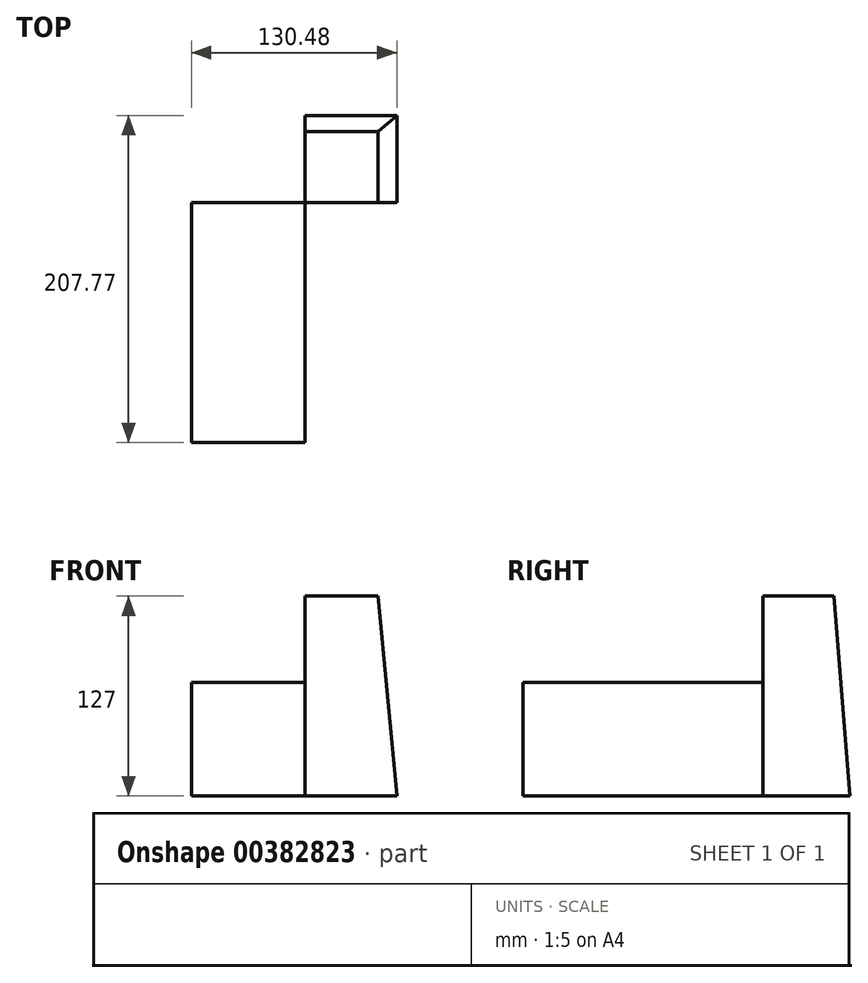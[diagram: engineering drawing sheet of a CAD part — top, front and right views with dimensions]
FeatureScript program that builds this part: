
annotation { "Feature Type Name" : "Feature", "Feature Type Description" : "" }
export const myFeature = defineFeature(function(context is Context, id is Id, definition is map)
    precondition{}
    {
        {
            var Q0;
            Q0=qCreatedBy(makeId("Top.planeOp"),FACE);
            var sketch = newSketch(context, id + "F0", { "sketchPlane" : qUnion([Q0])});
            skLineSegment(sketch, "E0.bottom", {"start": v(0, 0) * mm, "end": v(58.32, 0) * mm});
            skLineSegment(sketch, "E0.top", {"start": v(0, 55.37) * mm, "end": v(58.32, 55.37) * mm});
            skLineSegment(sketch, "E0.left", {"start": v(0, 0) * mm, "end": v(0, 55.37) * mm});
            skLineSegment(sketch, "E0.right", {"start": v(58.32, 0) * mm, "end": v(58.32, 55.37) * mm});
            skSolve(sketch);
        }
        {
            var Q0;
            Q0=qCreatedBy(makeId("Top.planeOp"),FACE);
            cPlane(context, id + "F1", {"entities" : qUnion([Q0]), "cplaneType" : CPlaneType.OFFSET, "offset" : 127 * mm, "width" : 152.4 * mm, "height" : 152.4 * mm});
        }
        {
            var Q0;
            Q0=qCreatedBy(id+"F1.planeOp",FACE);
            var sketch = newSketch(context, id + "F2", { "sketchPlane" : qUnion([Q0])});
            skLineSegment(sketch, "E1.bottom", {"start": v(0, 0) * mm, "end": v(46.25, 0) * mm});
            skLineSegment(sketch, "E1.top", {"start": v(0, 45.1) * mm, "end": v(46.25, 45.1) * mm});
            skLineSegment(sketch, "E1.left", {"start": v(0, 0) * mm, "end": v(0, 45.1) * mm});
            skLineSegment(sketch, "E1.right", {"start": v(46.25, 0) * mm, "end": v(46.25, 45.1) * mm});
            skSolve(sketch);
        }
        {
            var Q0;
            Q0=makeQuery(id+"F0.imprint","IMPRINT",FACE,{"disambiguationData":[TD([[makeQuery(id+"F0.imprint","IMPRINT",EDGE,{"derivedFrom":sQuery(id+"F0.wireOp",EDGE,"E0.bottom")}),1.0]])]});
            var Q1;
            Q1=makeQuery(id+"F2.imprint","IMPRINT",FACE,{"disambiguationData":[TD([[makeQuery(id+"F2.imprint","IMPRINT",EDGE,{"derivedFrom":sQuery(id+"F2.wireOp",EDGE,"E1.bottom")}),1.0]])]});
            loft(context, id + "F3", {"sheetProfilesArray" : [{ "sheetProfileEntities" : qUnion([Q0]) }, { "sheetProfileEntities" : qUnion([Q1]) }]});
        }
        {
            var Q0;
            Q0=qCreatedBy(makeId("Front.planeOp"),FACE);
            var sketch = newSketch(context, id + "F4", { "sketchPlane" : qUnion([Q0])});
            skLineSegment(sketch, "E2.bottom", {"start": v(0, 0) * mm, "end": v(-72.16, 0) * mm});
            skLineSegment(sketch, "E2.top", {"start": v(0, 72.26) * mm, "end": v(-72.16, 72.26) * mm});
            skLineSegment(sketch, "E2.left", {"start": v(0, 0) * mm, "end": v(0, 72.26) * mm});
            skLineSegment(sketch, "E2.right", {"start": v(-72.16, 0) * mm, "end": v(-72.16, 72.26) * mm});
            skSolve(sketch);
        }
        {
            var Q0;
            Q0 = qSketchRegion(id + "F4", true);
            extrude(context, id + "F5", {"entities" : qUnion([Q0]), "depth" : 152.4 * mm});
        }
    });
